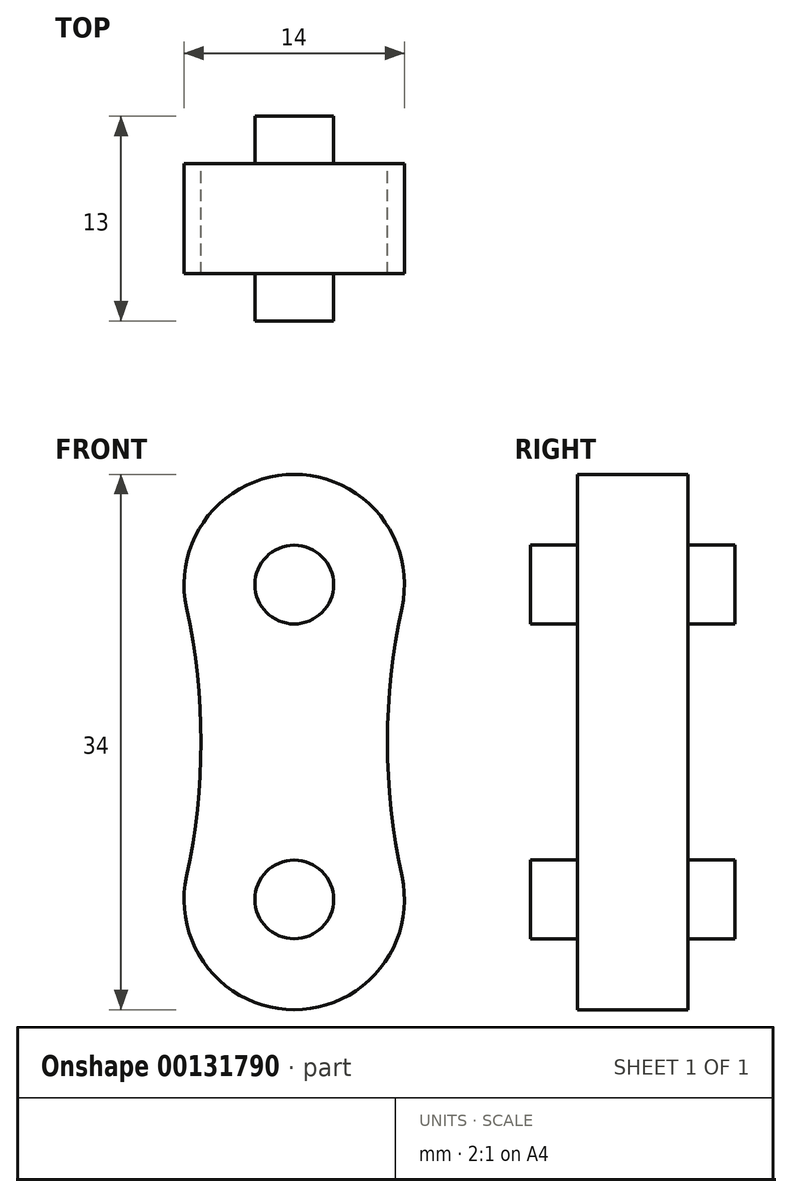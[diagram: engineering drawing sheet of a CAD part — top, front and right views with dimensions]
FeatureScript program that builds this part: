
annotation { "Feature Type Name" : "Feature", "Feature Type Description" : "" }
export const myFeature = defineFeature(function(context is Context, id is Id, definition is map)
    precondition{}
    {
        {
            var Q0;
            Q0=qCreatedBy(makeId("Front.planeOp"),FACE);
            var sketch = newSketch(context, id + "F0", { "sketchPlane" : qUnion([Q0])});
            skArc(sketch, "E0", {"start": v(54.52, 13.58) * mm, "mid": v(61.36, 5.09) * mm, "end": v(68.2, 13.58) * mm});
            skArc(sketch, "E1", {"start": v(68.2, 30.6) * mm, "mid": v(67.28, 22.09) * mm, "end": v(68.2, 13.58) * mm});
            skArc(sketch, "E2.MirrorC", {"start": v(54.52, 30.6) * mm, "mid": v(55.43, 22.09) * mm, "end": v(54.52, 13.58) * mm});
            skArc(sketch, "E3", {"start": v(68.2, 30.6) * mm, "mid": v(61.36, 39.1) * mm, "end": v(54.52, 30.6) * mm});
            skCircle(sketch, "E4", {"center": v(61.36, 32.1) * mm, "radius": 2.5 * mm});
            skCircle(sketch, "E5", {"center": v(61.36, 12.09) * mm, "radius": 2.5 * mm});
            skSolve(sketch);
        }
        {
            var Q0;
            Q0=makeQuery(id+"F0.imprint","IMPRINT",FACE,{"disambiguationData":[TD([[makeQuery(id+"F0.imprint","IMPRINT",EDGE,{"derivedFrom":sQuery(id+"F0.wireOp",EDGE,"E0")}),1.0]])]});
            extrude(context, id + "F1", {"entities" : qUnion([Q0]), "endBound" : BoundingType.SYMMETRIC, "depth" : 7 * mm});
        }
        {
            var Q0;
            Q0=qCreatedBy(makeId("Front.planeOp"),FACE);
            var sketch = newSketch(context, id + "F2", { "sketchPlane" : qUnion([Q0])});
            skCircle(sketch, "E6", {"center": v(61.36, 32.1) * mm, "radius": 2.5 * mm});
            skCircle(sketch, "E7", {"center": v(61.36, 12.09) * mm, "radius": 2.5 * mm});
            skSolve(sketch);
        }
        {
            var Q0;
            Q0 = qSketchRegion(id + "F2", true);
            extrude(context, id + "F3", {"entities" : qUnion([Q0]), "operationType" : NewBodyOperationType.ADD, "endBound" : BoundingType.SYMMETRIC, "depth" : 13 * mm});
        }
    });
